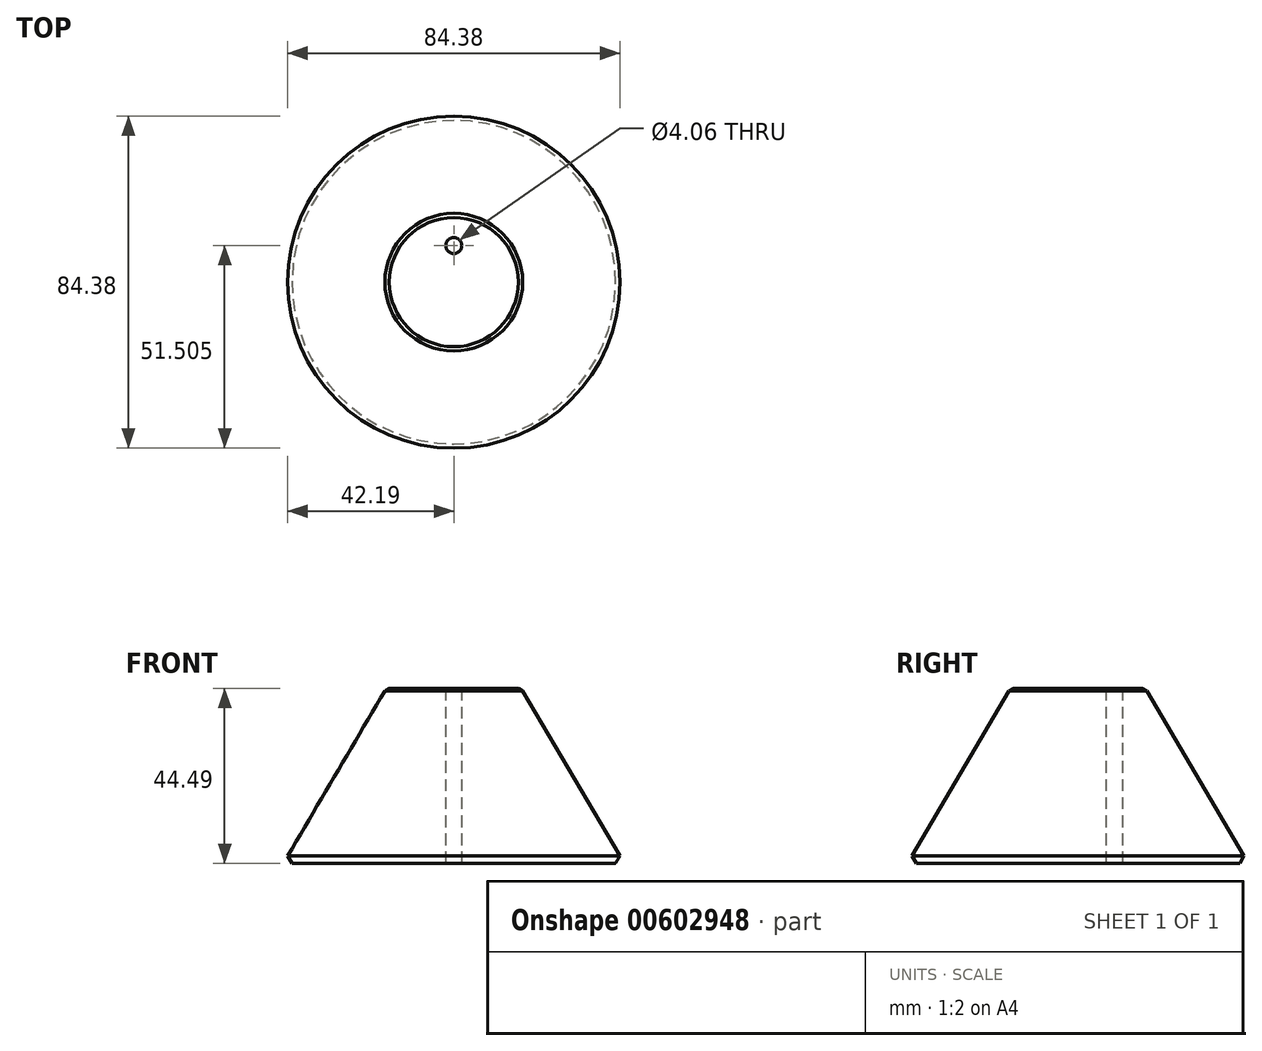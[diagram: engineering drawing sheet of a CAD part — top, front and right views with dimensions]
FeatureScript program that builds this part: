
annotation { "Feature Type Name" : "Feature", "Feature Type Description" : "" }
export const myFeature = defineFeature(function(context is Context, id is Id, definition is map)
    precondition{}
    {
        {
            var Q0;
            Q0=qCreatedBy(makeId("Front.planeOp"),FACE);
            var sketch = newSketch(context, id + "F0", { "sketchPlane" : qUnion([Q0])});
            skLineSegment(sketch, "E0", {"start": v(17.12, 44.5) * mm, "end": v(43.31, 0) * mm});
            skLineSegment(sketch, "E1", {"start": v(17.12, 0) * mm, "end": v(43.31, 0) * mm});
            skLineSegment(sketch, "E2", {"start": v(17.12, 44.5) * mm, "end": v(0, 44.5) * mm});
            skLineSegment(sketch, "E3", {"start": v(17.12, 0) * mm, "end": v(0, 0) * mm});
            skLineSegment(sketch, "E4", {"start": v(0, 0) * mm, "end": v(0, 44.5) * mm});
            skSolve(sketch);
        }
        {
            var Q0;
            Q0=makeQuery(id+"F0.imprint","IMPRINT",FACE,{"disambiguationData":[TD([[makeQuery(id+"F0.imprint","IMPRINT",EDGE,{"derivedFrom":sQuery(id+"F0.wireOp",EDGE,"E0")}),-1.0]])]});
            var Q1;
            Q1=sQuery(id+"F0.wireOp",EDGE,"E4");
            revolve(context, id + "F1", {"entities" : qUnion([Q0]), "axis" : qUnion([Q1]), "revolveType" : RevolveType.FULL});
        }
        {
            var Q0;
            Q0=makeQuery(id+"F1.opRevolve","SWEPT_FACE",FACE,{"disambiguationData":[OSD([sQuery(id+"F0.wireOp",EDGE,"E2")])]});
            var Q1;
            Q1=makeQuery(id+"F1.opRevolve","SWEPT_EDGE",EDGE,{"disambiguationData":[OSD([sQuery(id+"F0.wireOp",EDGE,"E0"),sQuery(id+"F0.wireOp",EDGE,"E1")])]});
            chamfer(context, id + "F2", {"entities" : qUnion([Q0, Q1]), "width" : 1.27 * mm, "tangentPropagation" : true});
        }
        {
            var Q0;
            Q0=makeQuery(id+"F1.opRevolve","SWEPT_FACE",FACE,{"disambiguationData":[OSD([sQuery(id+"F0.wireOp",EDGE,"E2")])]});
            var sketch = newSketch(context, id + "F3", { "sketchPlane" : qUnion([Q0])});
            skCircle(sketch, "E5", {"center": v(0, 0) * mm, "radius": 9.74 * mm});
            skSolve(sketch);
        }
        {
            var Q0;
            Q0=makeQuery(id+"F3.imprint","IMPRINT",FACE,{"disambiguationData":[TD([[makeQuery(id+"F3.imprint","IMPRINT",EDGE,{"derivedFrom":sQuery(id+"F3.wireOp",EDGE,"E5")}),1.0]])]});
            var sketch = newSketch(context, id + "F4", { "sketchPlane" : qUnion([Q0])});
            skCircle(sketch, "E6", {"center": v(0, 9.31) * mm, "radius": 2.03 * mm});
            skSolve(sketch);
        }
        {
            var Q0;
            Q0 = qSketchRegion(id + "F4", true);
            extrude(context, id + "F5", {"entities" : qUnion([Q0]), "operationType" : NewBodyOperationType.REMOVE, "endBound" : BoundingType.THROUGH_ALL, "oppositeDirection" : true, "depth" : 25 * mm, "offsetDistance" : 25 * mm});
        }
    });
